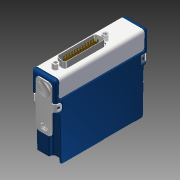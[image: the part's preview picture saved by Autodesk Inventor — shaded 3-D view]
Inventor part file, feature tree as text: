
AUTODESK INVENTOR PART (.ipt)
format: ipt  version: 2011 (Build 150239000, 239)  size: 6,139,392 bytes
history: native  units: mm
features: other x3, extrude x3, sketch x2, plane x2, imported_body x1, fillet x1
ambient origin geometry x8: Origin, YZ Plane, XZ Plane, XY Plane, X Axis, Y Axis, Z Axis, Center Point
bodies: Solid1 (feature_tree)
feature tree (12):
  imported_body  "Base1"
  other  "RIGHT"
  other  "TOP"
  other  "FRONT"
  sketch  "Sketch3"  dims[d22=5.08mm d23=0.0mm]
  extrude  "Extrusion2"  Depth=1.27mm TaperAngle=0.0deg
  extrude  "Extrusion3"  [1 undecoded]
  plane  "Work Plane4"
  plane  "Work Plane5"
  sketch  "Sketch2"  dims[d0=25.4mm d1=2.54mm d3=10.0mm d5=130.0mm d6=25.4mm d7=2.54mm d9=10.0mm d11=120.0mm d12=1.397mm d13=1.397mm d14=1.27mm d15=1.008245mm d17=0.0mm d18=25.4mm d19=0.381mm d20=1.27mm d21=0.0mm]
  fillet  "Fillet1"  [1 undecoded]
  extrude  "Extrusion1"  [1 undecoded]
note: 3 required parameter values undecoded (feature->parameter linkage not recoverable at this tier; creation-order binding heuristic only, values carry confidence <= 0.55)
